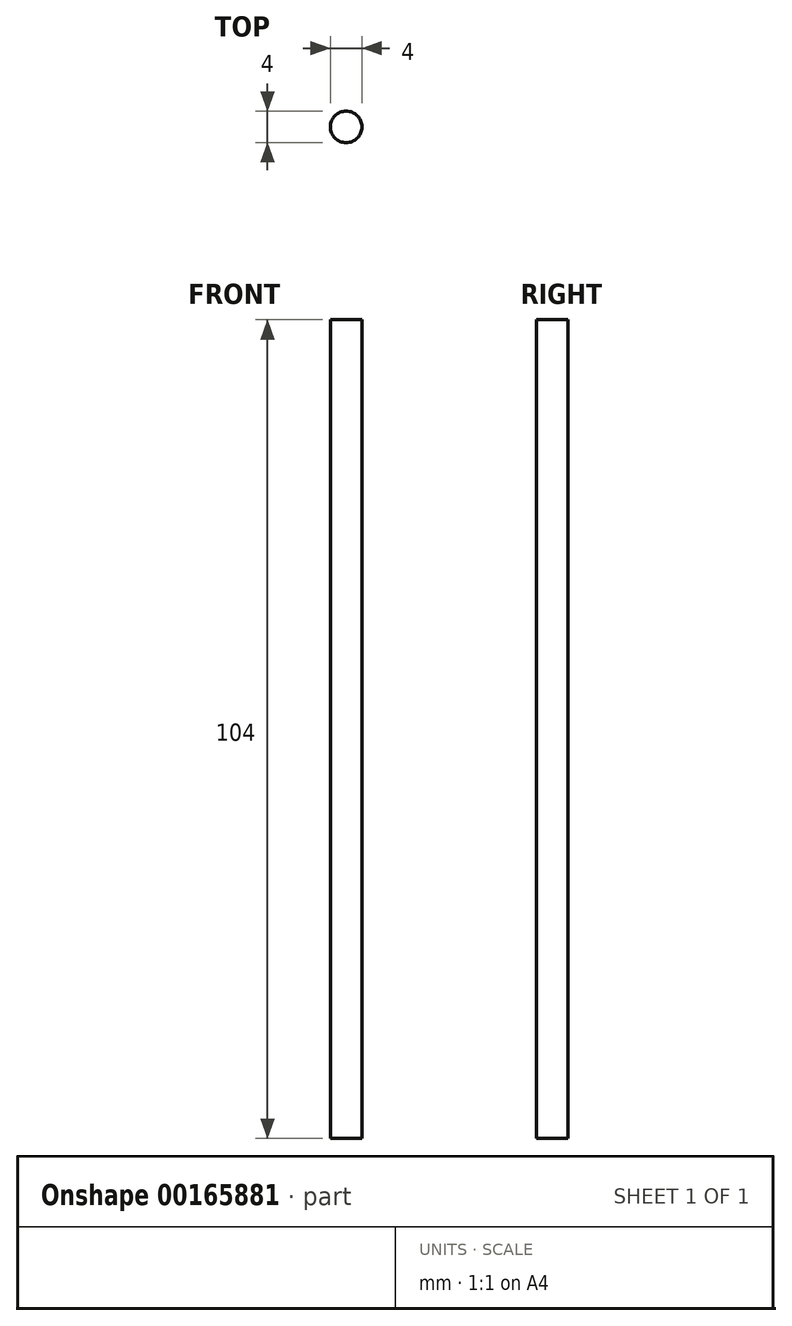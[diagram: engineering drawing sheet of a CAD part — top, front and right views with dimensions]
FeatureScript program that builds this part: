
annotation { "Feature Type Name" : "Feature", "Feature Type Description" : "" }
export const myFeature = defineFeature(function(context is Context, id is Id, definition is map)
    precondition{}
    {
        {
            var Q0;
            Q0=qCreatedBy(makeId("Top.planeOp"),FACE);
            var sketch = newSketch(context, id + "F0", { "sketchPlane" : qUnion([Q0])});
            skCircle(sketch, "E0", {"center": v(0, 0) * mm, "radius": 2 * mm});
            skSolve(sketch);
        }
        {
            var Q0;
            Q0 = qSketchRegion(id + "F0", true);
            extrude(context, id + "F1", {"entities" : qUnion([Q0]), "depth" : 104 * mm});
        }
    });
